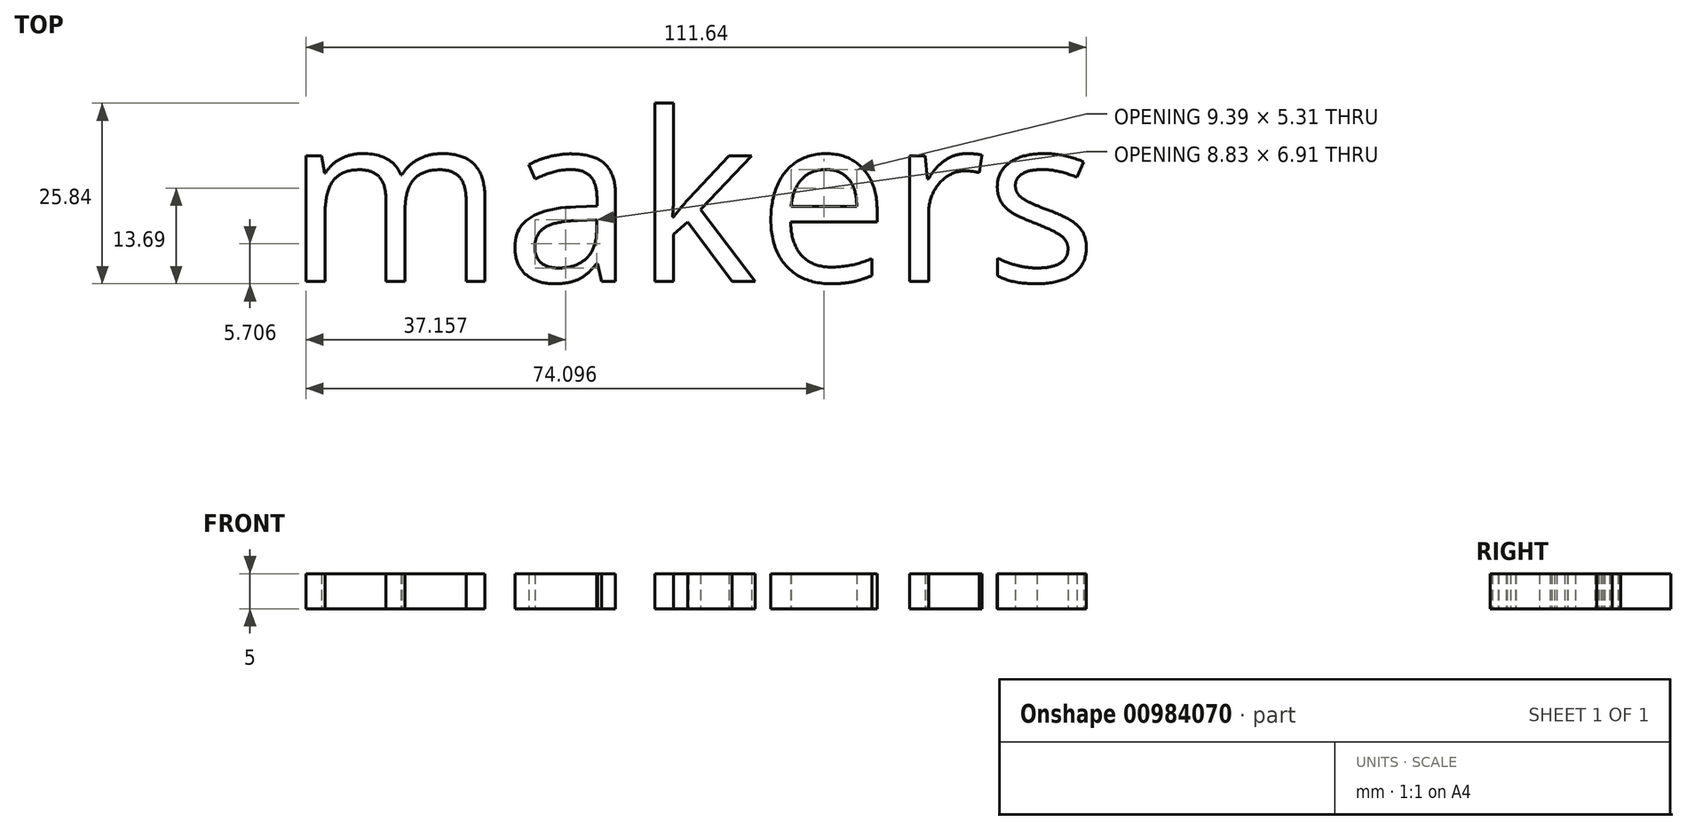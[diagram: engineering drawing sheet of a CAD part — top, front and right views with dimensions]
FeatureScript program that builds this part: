
annotation { "Feature Type Name" : "Feature", "Feature Type Description" : "" }
export const myFeature = defineFeature(function(context is Context, id is Id, definition is map)
    precondition{}
    {
        {
            var Q0;
            Q0=qCreatedBy(makeId("Top.planeOp"),FACE);
            var sketch = newSketch(context, id + "F0", { "sketchPlane" : qUnion([Q0])});
            skText(sketch, "E0", { "text": "makers", "fontName": "OpenSans-Regular.ttf"});
            const initialGuessF0  = {"E0": [0, 0, 1, 0, 0.02417]};
            skSetInitialGuess(sketch, initialGuessF0);
            skSolve(sketch);
        }
        {
            var Q0;
            Q0 = qSketchRegion(id + "F0", true);
            extrude(context, id + "F1", {"entities" : qUnion([Q0]), "depth" : 5 * mm, "offsetDistance" : 25 * mm});
        }
    });
